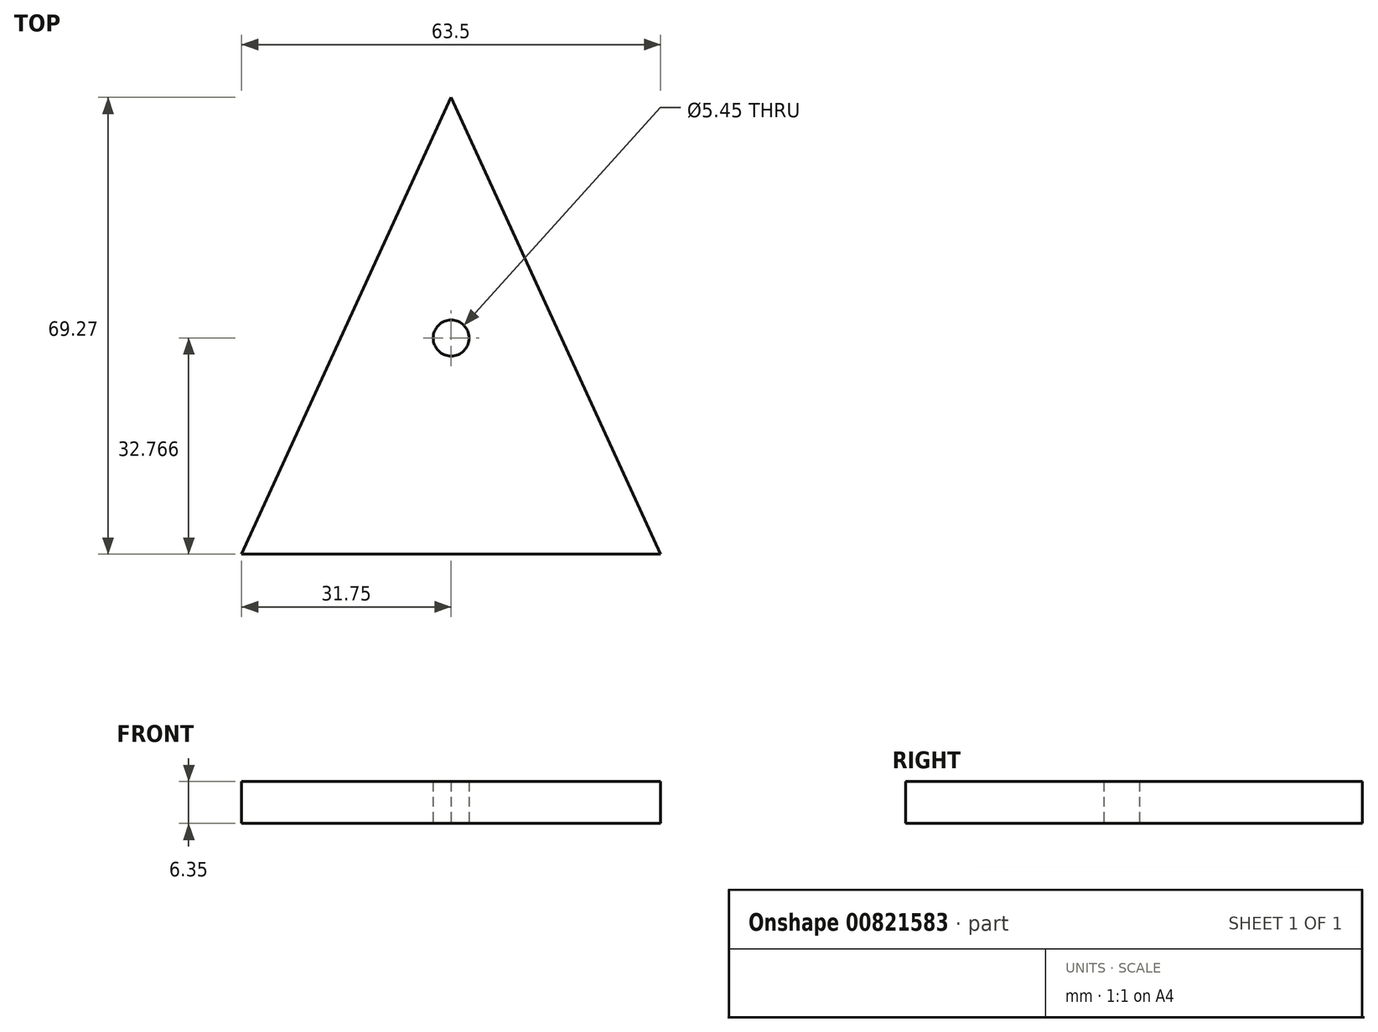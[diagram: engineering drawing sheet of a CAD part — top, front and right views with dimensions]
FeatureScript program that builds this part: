
annotation { "Feature Type Name" : "Feature", "Feature Type Description" : "" }
export const myFeature = defineFeature(function(context is Context, id is Id, definition is map)
    precondition{}
    {
        {
            var Q0;
            Q0=qCreatedBy(makeId("Top.planeOp"),FACE);
            var sketch = newSketch(context, id + "F0", { "sketchPlane" : qUnion([Q0])});
            skLineSegment(sketch, "E0", {"start": v(0, 34.76) * mm, "end": v(-31.75, -34.51) * mm});
            skLineSegment(sketch, "E1", {"start": v(-31.75, -34.51) * mm, "end": v(31.75, -34.51) * mm});
            skLineSegment(sketch, "E2", {"start": v(31.75, -34.51) * mm, "end": v(0, 34.76) * mm});
            skCircle(sketch, "E3", {"center": v(0, -1.74) * mm, "radius": 2.72 * mm});
            skSolve(sketch);
        }
        {
            var Q0;
            Q0=makeQuery(id+"F0.imprint","IMPRINT",FACE,{"disambiguationData":[TD([[makeQuery(id+"F0.imprint","IMPRINT",EDGE,{"derivedFrom":sQuery(id+"F0.wireOp",EDGE,"E0")}),1.0]])]});
            extrude(context, id + "F1", {"entities" : qUnion([Q0]), "depth" : 6.35 * mm, "offsetDistance" : 25.4 * mm});
        }
    });
